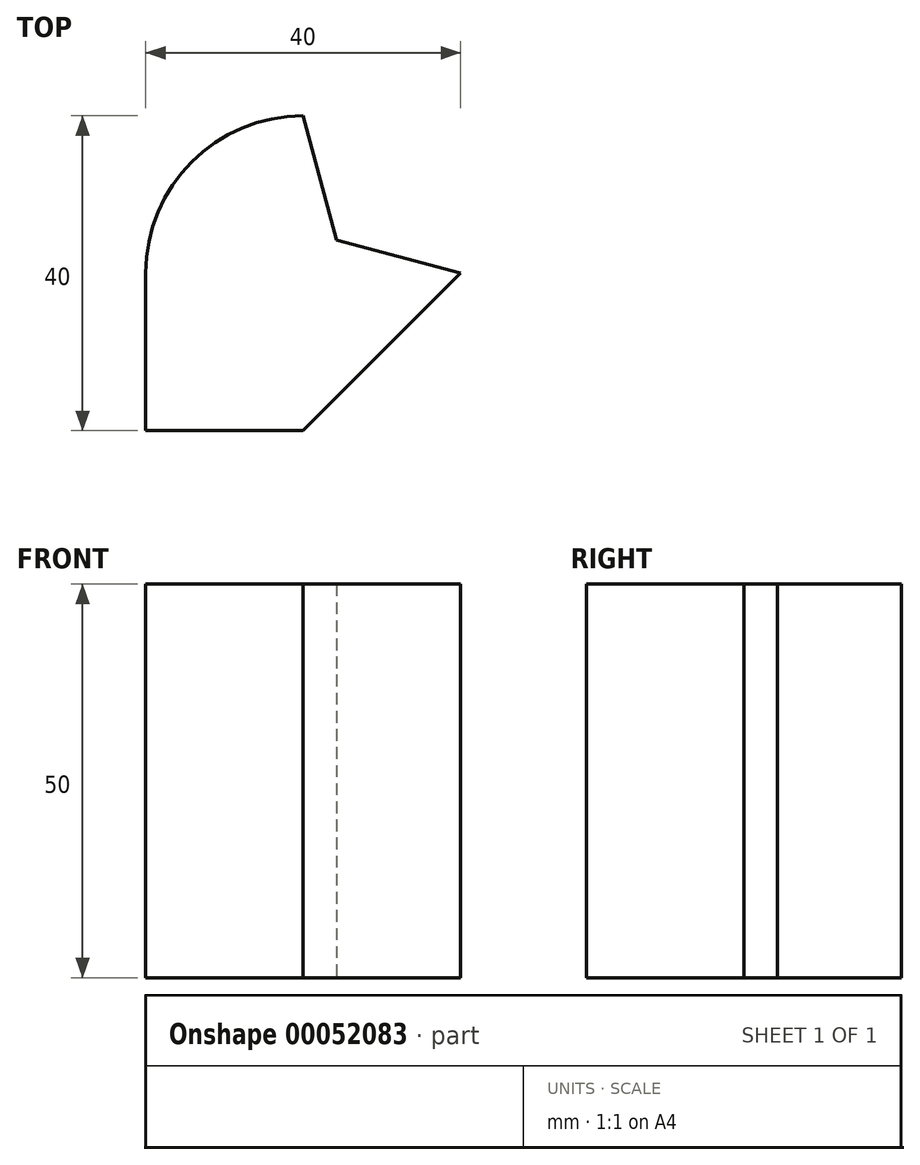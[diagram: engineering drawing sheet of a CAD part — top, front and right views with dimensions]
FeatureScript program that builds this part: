
annotation { "Feature Type Name" : "Feature", "Feature Type Description" : "" }
export const myFeature = defineFeature(function(context is Context, id is Id, definition is map)
    precondition{}
    {
        {
            var Q0;
            Q0=qCreatedBy(makeId("Top.planeOp"),FACE);
            var sketch = newSketch(context, id + "F0", { "sketchPlane" : qUnion([Q0])});
            skLineSegment(sketch, "E0", {"start": v(-20, 0) * mm, "end": v(-20, -20) * mm});
            skLineSegment(sketch, "E1", {"start": v(-20, -20) * mm, "end": v(0, -20) * mm});
            skLineSegment(sketch, "E2", {"start": v(0, -20) * mm, "end": v(20, 0) * mm});
            skLineSegment(sketch, "E3", {"start": v(20, 0) * mm, "end": v(4.23, 4.23) * mm});
            skLineSegment(sketch, "E4", {"start": v(4.23, 4.23) * mm, "end": v(0, 20) * mm});
            skLineSegment(sketch, "E5", {"start": v(4.23, 4.23) * mm, "end": v(-20, -20) * mm, "construction": true});
            skArc(sketch, "E6", {"start": v(0, 20) * mm, "mid": v(-14.14, 14.14) * mm, "end": v(-20, 0) * mm});
            skSolve(sketch);
        }
        {
            var Q0;
            Q0 = qSketchRegion(id + "F0", true);
            extrude(context, id + "F1", {"entities" : qUnion([Q0]), "depth" : 50 * mm});
        }
    });
